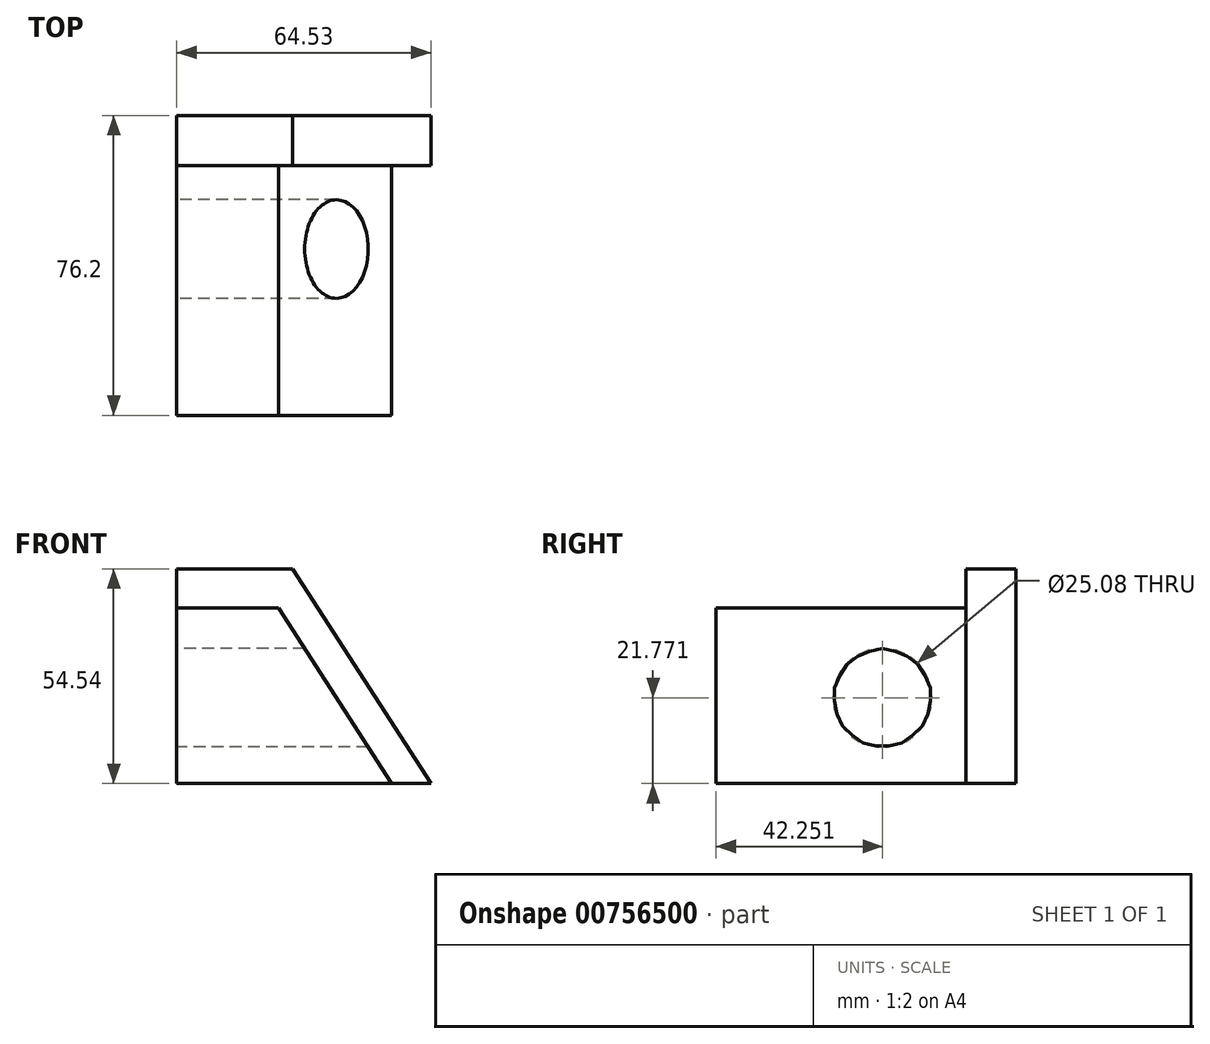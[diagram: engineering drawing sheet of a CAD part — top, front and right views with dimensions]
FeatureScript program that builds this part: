
annotation { "Feature Type Name" : "Feature", "Feature Type Description" : "" }
export const myFeature = defineFeature(function(context is Context, id is Id, definition is map)
    precondition{}
    {
        {
            var Q0;
            Q0=qCreatedBy(makeId("Front.planeOp"),FACE);
            var sketch = newSketch(context, id + "F0", { "sketchPlane" : qUnion([Q0])});
            skLineSegment(sketch, "E0", {"start": v(0, 0) * mm, "end": v(-54.6, 0) * mm});
            skLineSegment(sketch, "E1", {"start": v(-54.6, 0) * mm, "end": v(-54.6, 44.62) * mm});
            skLineSegment(sketch, "E2", {"start": v(-54.6, 44.62) * mm, "end": v(-28.78, 44.62) * mm});
            skLineSegment(sketch, "E3", {"start": v(-28.78, 44.62) * mm, "end": v(0, 0) * mm});
            skSolve(sketch);
        }
        {
            var Q0;
            Q0=makeQuery(id+"F0.imprint","IMPRINT",FACE,{"disambiguationData":[TD([[makeQuery(id+"F0.imprint","IMPRINT",EDGE,{"derivedFrom":sQuery(id+"F0.wireOp",EDGE,"E0")}),-1.0]])]});
            var sketch = newSketch(context, id + "F1", { "sketchPlane" : qUnion([Q0])});
            skSolve(sketch);
        }
        {
            var Q0;
            Q0 = qSketchRegion(id + "F1", true);
            var Q1;
            Q1=makeQuery(id+"F0.imprint","IMPRINT",FACE,{"disambiguationData":[TD([[makeQuery(id+"F0.imprint","IMPRINT",EDGE,{"derivedFrom":sQuery(id+"F0.wireOp",EDGE,"E0")}),-1.0]])]});
            extrude(context, id + "F2", {"entities" : qUnion([Q0, Q1]), "depth" : 76.2 * mm, "offsetDistance" : 25.4 * mm});
        }
        {
            var Q0;
            Q0=makeQuery(id+"F2.opExtrude","SWEPT_FACE",FACE,{"disambiguationData":[OSD([sQuery(id+"F0.wireOp",EDGE,"E1")])]});
            var sketch = newSketch(context, id + "F3", { "sketchPlane" : qUnion([Q0])});
            skCircle(sketch, "E4", {"center": v(33.95, 21.77) * mm, "radius": 12.54 * mm});
            skSolve(sketch);
        }
        {
            var Q0;
            Q0 = qSketchRegion(id + "F3", true);
            extrude(context, id + "F4", {"entities" : qUnion([Q0]), "operationType" : NewBodyOperationType.REMOVE, "endBound" : BoundingType.THROUGH_ALL, "oppositeDirection" : true, "depth" : 25.4 * mm, "offsetDistance" : 25.4 * mm});
        }
        {
            var Q0;
            Q0=qCreatedBy(makeId("Front.planeOp"),FACE);
            var sketch = newSketch(context, id + "F5", { "sketchPlane" : qUnion([Q0])});
            skLineSegment(sketch, "E5", {"start": v(-54.6, 44.62) * mm, "end": v(-54.6, 54.54) * mm});
            skLineSegment(sketch, "E6", {"start": v(-54.6, 54.54) * mm, "end": v(-25.26, 54.54) * mm});
            skLineSegment(sketch, "E7", {"start": v(-25.26, 54.54) * mm, "end": v(9.92, 0) * mm});
            skLineSegment(sketch, "E8", {"start": v(9.92, 0) * mm, "end": v(0, 0) * mm});
            skLineSegment(sketch, "E9", {"start": v(0, 0) * mm, "end": v(-28.78, 44.62) * mm});
            skLineSegment(sketch, "E10", {"start": v(-28.78, 44.62) * mm, "end": v(-54.6, 44.62) * mm});
            skSolve(sketch);
        }
        {
            var Q0;
            Q0 = qSketchRegion(id + "F5", true);
            extrude(context, id + "F6", {"entities" : qUnion([Q0]), "operationType" : NewBodyOperationType.ADD, "depth" : 12.7 * mm, "offsetDistance" : 25.4 * mm});
        }
    });
